# Revit family: Lighting_Pendants_Nordlux_Nexus_2.0
name_source: partatom
category: Lighting Fixtures
revit_build: Autodesk Revit 2017 (Build: 20190508_0315(x64)
units: mm (PartAtom-declared; Revit-internal decimal feet)

## family parameters
Always vertical = Yes
Cut with Voids When Loaded = No
Host = Ceiling
Light Source = Yes
OmniClass Number = 23.80.70.11
OmniClass Title = Luminaries for Internal Lighting
Part Type = Normal
Room Calculation Point = No
Round Connector Dimension = Use Diameter
Shared = No

## types (2) — shared parameters
AssetType = Fixed
BIMObjectName = Lighting_Pendants_Nordlux_Nexus_2.0
Brand = Nordlux
Category = Indoor lighting
Collection = Nexus 2.0
Color Filter = 16777215
ConvergoRefNr = 0143-1909-0010-DK
Description = NEXUS is an exciting series that epitomises Nordic cool. The details tell the story of an elegantly designed light, for example, the pendant’s invisible transition between shade and cord, and the beautiful enclosed acrylic inserts that create an exciting play of light.
Designer = Bonnelycke MDD
Dimming Lamp Color Temperature Shift = <None>
DurationUnit = Hours
Emit Shape Visible in Rendering = No
Emit from Circle Diameter = 50 mm  [stored 0.164042 ft]
EnergyClass = A++ - D
Features = Includes acylic diffuser. Textile cable 250cm. Cable can not be replaced.
Finish = Satin soft, matt surface. Ex. acrylic patton diffuser. Primary material metal, secondary material plastic, textile cable
HasProtectiveEarth = No
IP_Code = IP20
IfcExportAs = IfcLightFixtureType
IfcExportType = NOTDEFINED
InsulationStandardClass = Class 2 (Double isolated)
LensMaterial = Acrylic diffuser
LightFixtureMountingType = Suspended
LightFixturePlacingType = Ceilling
LightFixtureTertiaryMaterial = Glass
LightSource = Not included
Manufacturer = Nordlux
ManufacturerName = Nordlux
ManufacturerURL = https://www.nordlux.com
Material = Metal, plastic & textile
NBSDescription = General purpose luminaires
NBSReference = 90-60-50/405
Name = Nordlux_Nexus_2.0
NominalCurrent = 0 A
NominalDiameter = 200 mm  [stored 0.656168 ft]
NominalFrequencyRange = 50 Hz
NominalLength = 200 mm  [stored 0.656168 ft]
NominalRadius = 100 mm  [stored 0.328084 ft]
NominalVoltage = 230 V
NominalVoltageCalc = 0 V
NominalWidth = 200 mm  [stored 0.656168 ft]
NumberOfPoles = 1
PhaseAngle = 0.00°
Photometric Web File = 7726 Nexus 20 Pendel w acryl.ies
Product data url = https://www.bimobject.com
ProductDatasheet = http://pim.skypim.com
Revision = 1
Shape = Sculptured
Size = Shade: 200x200x250 mm / Canopy: 120x120x90 mm
Socket = E27
Tilt Angle = 90.00°
TotalWattage = 40 W
URL = https://www.nordlux.com
Uniclass2 = Pr_70_70_49_86
Uniclass2015Description = Pendant  luminaires
Uniclass2015Reference = Pr_70_70_48_62
UsageCurrent = 0 A
Version = 2
VersionDate = 01/07/2020
WarrantyDurationUnit = Hours
zero-valued in all types: DefaultElevation, ElectricalDeviceNominalPower, MaintenanceFactor, NumberOfSources

## per-type parameters (varying)
| type | ArticleNumber | Color | EANNumber | LightFixtureMainMaterial | LightFixtureSecondaryMaterial | ModelReference |
| Nexus 2.0 Pendant - white | 2020583001 | White RAL7047 | 5704924002342 | White | White cable | 2020583001 |
| Nexus 2.0 Pendant - black | 2020583003 | Black RAL9005 | 5704924002359 | Black | Black cable | 2020583003 |

note: column(s) folded — value = type name in every type: Model

note: [stored X ft] marks values corroborated as IEEE doubles in the binary element streams (Revit-internal decimal feet)

## geometry (parser evidence)
native form markers: Sweep x8
no freeform markers — native parametric forms only
